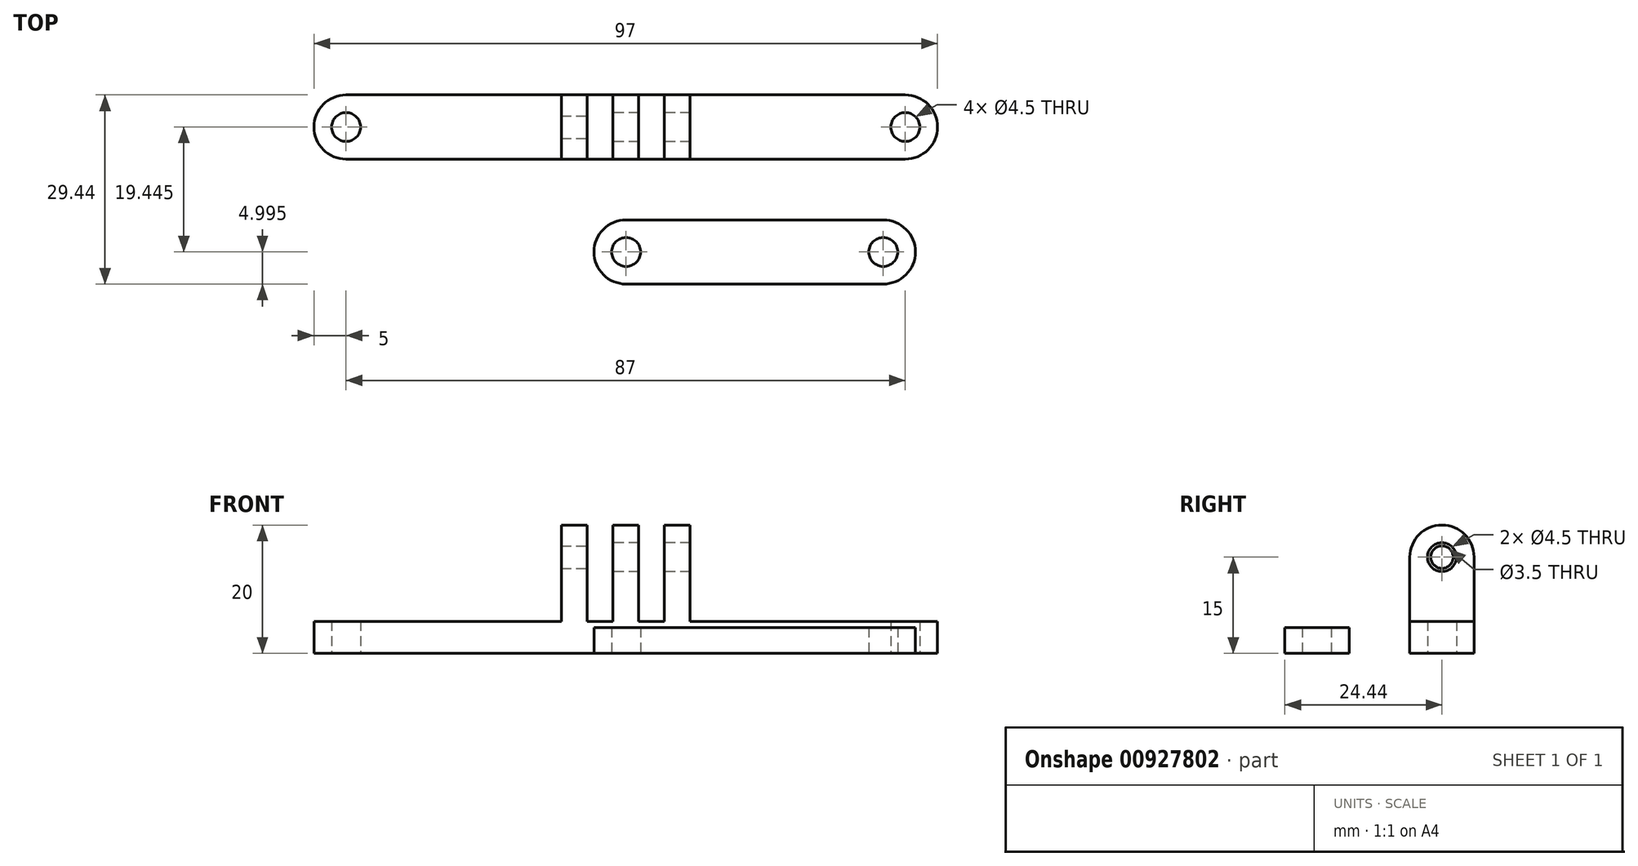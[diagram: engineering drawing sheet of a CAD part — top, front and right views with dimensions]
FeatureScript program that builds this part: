
annotation { "Feature Type Name" : "Feature", "Feature Type Description" : "" }
export const myFeature = defineFeature(function(context is Context, id is Id, definition is map)
    precondition{}
    {
        {
            var Q0;
            Q0=qCreatedBy(makeId("Front.planeOp"),FACE);
            var sketch = newSketch(context, id + "F0", { "sketchPlane" : qUnion([Q0])});
            skLineSegment(sketch, "E0.bottom", {"start": v(-48.5, 0) * mm, "end": v(48.5, 0) * mm});
            skLineSegment(sketch, "E0.top", {"start": v(-48.5, 5) * mm, "end": v(48.5, 5) * mm});
            skLineSegment(sketch, "E0.left", {"start": v(-48.5, 0) * mm, "end": v(-48.5, 5) * mm});
            skLineSegment(sketch, "E0.right", {"start": v(48.5, 0) * mm, "end": v(48.5, 5) * mm});
            skLineSegment(sketch, "E1.bottom", {"start": v(-10, 5) * mm, "end": v(-6, 5) * mm});
            skLineSegment(sketch, "E1.top", {"start": v(-10, 20) * mm, "end": v(-6, 20) * mm});
            skLineSegment(sketch, "E1.left", {"start": v(-10, 5) * mm, "end": v(-10, 20) * mm});
            skLineSegment(sketch, "E1.right", {"start": v(-6, 5) * mm, "end": v(-6, 20) * mm});
            skLineSegment(sketch, "E2.1.0.0", {"start": v(-2, 5) * mm, "end": v(-2, 20) * mm});
            skLineSegment(sketch, "E2.1.0.1", {"start": v(-2, 20) * mm, "end": v(2, 20) * mm});
            skLineSegment(sketch, "E2.1.0.2", {"start": v(2, 5) * mm, "end": v(2, 20) * mm});
            skLineSegment(sketch, "E2.2.0.0", {"start": v(6, 5) * mm, "end": v(6, 20) * mm});
            skLineSegment(sketch, "E2.2.0.1", {"start": v(6, 20) * mm, "end": v(10, 20) * mm});
            skLineSegment(sketch, "E2.2.0.2", {"start": v(10, 5) * mm, "end": v(10, 20) * mm});
            skLineSegment(sketch, "E2.direction1", {"start": v(-10, 5) * mm, "end": v(-2, 5) * mm, "construction": true});
            skLineSegment(sketch, "E3", {"start": v(0, 0) * mm, "end": v(0, 20) * mm, "construction": true});
            skSolve(sketch);
        }
        {
            var Q0;
            {var subQ0=sQuery(id+"F0.wireOp",EDGE,"E2.1.0.0");Q0=makeQuery(id+"F0.imprint","IMPRINT",FACE,{"disambiguationData":[TD([[makeQuery(id+"F0.imprint","IMPRINT",EDGE,{"derivedFrom":subQ0}),-1.0]])]});}
            var Q1;
            {var subQ0=sQuery(id+"F0.wireOp",EDGE,"E2.2.0.0");Q1=makeQuery(id+"F0.imprint","IMPRINT",FACE,{"disambiguationData":[TD([[makeQuery(id+"F0.imprint","IMPRINT",EDGE,{"derivedFrom":subQ0}),-1.0]])]});}
            var Q2;
            Q2=makeQuery(id+"F0.imprint","IMPRINT",FACE,{"disambiguationData":[TD([[makeQuery(id+"F0.imprint","IMPRINT",EDGE,{"derivedFrom":sQuery(id+"F0.wireOp",EDGE,"E1.top")}),-1.0]])]});
            var Q3;
            Q3=makeQuery(id+"F0.imprint","IMPRINT",FACE,{"disambiguationData":[TD([[makeQuery(id+"F0.imprint","IMPRINT",EDGE,{"derivedFrom":sQuery(id+"F0.wireOp",EDGE,"E0.bottom")}),1.0]])]});
            extrude(context, id + "F1", {"entities" : qUnion([Q0, Q1, Q2, Q3]), "endBound" : BoundingType.SYMMETRIC, "depth" : 10 * mm, "offsetDistance" : 25 * mm});
        }
        {
            var Q0;
            Q0=makeQuery(id+"F1.opExtrude","CAP_EDGE",EDGE,{"disambiguationData":[OSD([sQuery(id+"F0.wireOp",EDGE,"E0.left")])],"isStart":false});
            var Q1;
            Q1=makeQuery(id+"F1.opExtrude","CAP_EDGE",EDGE,{"disambiguationData":[OSD([sQuery(id+"F0.wireOp",EDGE,"E0.left")])],"isStart":true});
            var Q2;
            Q2=makeQuery(id+"F1.opExtrude","CAP_EDGE",EDGE,{"disambiguationData":[OSD([sQuery(id+"F0.wireOp",EDGE,"E0.right")])],"isStart":false});
            var Q3;
            Q3=makeQuery(id+"F1.opExtrude","CAP_EDGE",EDGE,{"disambiguationData":[OSD([sQuery(id+"F0.wireOp",EDGE,"E0.right")])],"isStart":true});
            var Q4;
            Q4=makeQuery(id+"F1.opExtrude","CAP_EDGE",EDGE,{"disambiguationData":[OSD([sQuery(id+"F0.wireOp",EDGE,"E1.top")])],"isStart":false});
            var Q5;
            Q5=makeQuery(id+"F1.opExtrude","CAP_EDGE",EDGE,{"disambiguationData":[OSD([sQuery(id+"F0.wireOp",EDGE,"E2.1.0.1")])],"isStart":false});
            var Q6;
            Q6=makeQuery(id+"F1.opExtrude","CAP_EDGE",EDGE,{"disambiguationData":[OSD([sQuery(id+"F0.wireOp",EDGE,"E2.2.0.1")])],"isStart":false});
            var Q7;
            Q7=makeQuery(id+"F1.opExtrude","CAP_EDGE",EDGE,{"disambiguationData":[OSD([sQuery(id+"F0.wireOp",EDGE,"E1.top")])],"isStart":true});
            var Q8;
            Q8=makeQuery(id+"F1.opExtrude","CAP_EDGE",EDGE,{"disambiguationData":[OSD([sQuery(id+"F0.wireOp",EDGE,"E2.1.0.1")])],"isStart":true});
            var Q9;
            Q9=makeQuery(id+"F1.opExtrude","CAP_EDGE",EDGE,{"disambiguationData":[OSD([sQuery(id+"F0.wireOp",EDGE,"E2.2.0.1")])],"isStart":true});
            fillet(context, id + "F2", {"entities" : qUnion([Q0, Q1, Q2, Q3, Q4, Q5, Q6, Q7, Q8, Q9]), "radius" : 5 * mm, "tangentPropagation" : true, "allowEdgeOverflow" : false});
        }
        {
            var Q0;
            Q0=makeQuery(id+"F1.opExtrude","SWEPT_FACE",FACE,{"disambiguationData":[OSD([sQuery(id+"F0.wireOp",EDGE,"E0.bottom")])]});
            var sketch = newSketch(context, id + "F3", { "sketchPlane" : qUnion([Q0])});
            skPoint(sketch, "E4", {"position": v(-43.5, 0) * mm});
            skPoint(sketch, "E5", {"position": v(43.5, 0) * mm});
            skLineSegment(sketch, "E6", {"start": v(0, 5) * mm, "end": v(0, -5) * mm, "construction": true});
            skSolve(sketch);
        }
        {
            var Q0;
            Q0=sQuery(id+"F3.wireOp",VERTEX,"E4");
            var Q1;
            Q1=sQuery(id+"F3.wireOp",VERTEX,"E5");
            var Q2;
            Q2=makeQuery(id+"F1.opExtrude","SWEPT_BODY",BODY,{"disambiguationData":[OSD([sQuery(id+"F0.wireOp",EDGE,"E0.bottom"),sQuery(id+"F0.wireOp",EDGE,"E0.top"),sQuery(id+"F0.wireOp",EDGE,"E0.left"),sQuery(id+"F0.wireOp",EDGE,"E0.right"),sQuery(id+"F0.wireOp",EDGE,"E1.top"),sQuery(id+"F0.wireOp",EDGE,"E1.left"),sQuery(id+"F0.wireOp",EDGE,"E1.right"),sQuery(id+"F0.wireOp",EDGE,"E2.1.0.0"),sQuery(id+"F0.wireOp",EDGE,"E2.1.0.1"),sQuery(id+"F0.wireOp",EDGE,"E2.1.0.2"),sQuery(id+"F0.wireOp",EDGE,"E2.2.0.0"),sQuery(id+"F0.wireOp",EDGE,"E2.2.0.1"),sQuery(id+"F0.wireOp",EDGE,"E2.2.0.2")])]});
            hole(context, id + "F4", {"style" : HoleStyle.SIMPLE, "endStyle" : HoleEndStyle.THROUGH, "standardTappedOrClearance" : lookupTablePath({ "fit" : "Normal", "standard" : "ISO", "size" : "M4", "type" : "Clearance" }), "standardBlindInLast" : lookupTablePath({ "fit" : "Normal", "standard" : "ISO", "engagement" : "75%", "pitch" : "0.7 mm", "size" : "M4", "type" : "Clearance & tapped" }), "holeDiameter" : 4.5 * mm, "majorDiameter" : 5 * mm, "isTappedThrough" : true, "tappedDepth" : 12 * mm, "tapClearance" : 3, "locations" : qUnion([Q0, Q1]), "scope" : qUnion([Q2])});
        }
        {
            var Q0;
            Q0=makeQuery(id+"F1.opExtrude","SWEPT_FACE",FACE,{"disambiguationData":[OSD([sQuery(id+"F0.wireOp",EDGE,"E2.1.0.0")])]});
            var sketch = newSketch(context, id + "F5", { "sketchPlane" : qUnion([Q0])});
            skPoint(sketch, "E7", {"position": v(0, 15) * mm});
            skSolve(sketch);
        }
        {
            var Q0;
            Q0=sQuery(id+"F5.wireOp",VERTEX,"E7");
            var Q1;
            Q1=makeQuery(id+"F1.opExtrude","SWEPT_BODY",BODY,{"disambiguationData":[OSD([sQuery(id+"F0.wireOp",EDGE,"E0.bottom"),sQuery(id+"F0.wireOp",EDGE,"E0.top"),sQuery(id+"F0.wireOp",EDGE,"E0.left"),sQuery(id+"F0.wireOp",EDGE,"E0.right"),sQuery(id+"F0.wireOp",EDGE,"E1.top"),sQuery(id+"F0.wireOp",EDGE,"E1.left"),sQuery(id+"F0.wireOp",EDGE,"E1.right"),sQuery(id+"F0.wireOp",EDGE,"E2.1.0.0"),sQuery(id+"F0.wireOp",EDGE,"E2.1.0.1"),sQuery(id+"F0.wireOp",EDGE,"E2.1.0.2"),sQuery(id+"F0.wireOp",EDGE,"E2.2.0.0"),sQuery(id+"F0.wireOp",EDGE,"E2.2.0.1"),sQuery(id+"F0.wireOp",EDGE,"E2.2.0.2")])]});
            hole(context, id + "F6", {"style" : HoleStyle.SIMPLE, "endStyle" : HoleEndStyle.THROUGH, "standardTappedOrClearance" : lookupTablePath({ "fit" : "Normal", "standard" : "ISO", "size" : "M4", "type" : "Clearance" }), "standardBlindInLast" : lookupTablePath({ "fit" : "Normal", "standard" : "ISO", "engagement" : "75%", "pitch" : "0.7 mm", "size" : "M4", "type" : "Clearance & tapped" }), "holeDiameter" : 4.5 * mm, "majorDiameter" : 5 * mm, "isTappedThrough" : true, "tappedDepth" : 12 * mm, "tapClearance" : 3, "locations" : qUnion([Q0]), "scope" : qUnion([Q1])});
        }
        {
            var Q0;
            Q0=sQuery(id+"F5.wireOp",VERTEX,"E7");
            var Q1;
            Q1=makeQuery(id+"F1.opExtrude","SWEPT_BODY",BODY,{"disambiguationData":[OSD([sQuery(id+"F0.wireOp",EDGE,"E0.bottom"),sQuery(id+"F0.wireOp",EDGE,"E0.top"),sQuery(id+"F0.wireOp",EDGE,"E0.left"),sQuery(id+"F0.wireOp",EDGE,"E0.right"),sQuery(id+"F0.wireOp",EDGE,"E1.top"),sQuery(id+"F0.wireOp",EDGE,"E1.left"),sQuery(id+"F0.wireOp",EDGE,"E1.right"),sQuery(id+"F0.wireOp",EDGE,"E2.1.0.0"),sQuery(id+"F0.wireOp",EDGE,"E2.1.0.1"),sQuery(id+"F0.wireOp",EDGE,"E2.1.0.2"),sQuery(id+"F0.wireOp",EDGE,"E2.2.0.0"),sQuery(id+"F0.wireOp",EDGE,"E2.2.0.1"),sQuery(id+"F0.wireOp",EDGE,"E2.2.0.2")])]});
            hole(context, id + "F7", {"style" : HoleStyle.SIMPLE, "endStyle" : HoleEndStyle.THROUGH, "oppositeDirection" : true, "standardTappedOrClearance" : lookupTablePath({ "standard" : "ISO", "size" : "3.5", "type" : "Drilled" }), "standardBlindInLast" : lookupTablePath({ "standard" : "ISO", "size" : "3.5", "type" : "Drilled" }), "holeDiameter" : 3.5 * mm, "majorDiameter" : 4 * mm, "isTappedThrough" : true, "tappedDepth" : 12 * mm, "tapClearance" : 3, "locations" : qUnion([Q0]), "scope" : qUnion([Q1])});
        }
        {
            var Q0;
            Q0=qCreatedBy(makeId("Top.planeOp"),FACE);
            var sketch = newSketch(context, id + "F8", { "sketchPlane" : qUnion([Q0])});
            skLineSegment(sketch, "E8.bottom", {"start": v(0.07, -14.44) * mm, "end": v(40.07, -14.44) * mm});
            skLineSegment(sketch, "E8.top", {"start": v(0.07, -24.44) * mm, "end": v(40.07, -24.44) * mm});
            skLineSegment(sketch, "E8.left", {"start": v(-4.93, -19.44) * mm, "end": v(-4.93, -19.44) * mm});
            skLineSegment(sketch, "E8.right", {"start": v(45.07, -19.44) * mm, "end": v(45.07, -19.44) * mm});
            skPoint(sketch, "E9.visualSharp", {"position": v(-4.93, -14.44) * mm});
            skArc(sketch, "E9.filletArc", {"start": v(0.07, -14.44) * mm, "mid": v(-3.47, -15.9) * mm, "end": v(-4.93, -19.44) * mm});
            skPoint(sketch, "E10.visualSharp", {"position": v(-4.93, -24.44) * mm});
            skArc(sketch, "E10.filletArc", {"start": v(-4.93, -19.44) * mm, "mid": v(-3.47, -22.98) * mm, "end": v(0.07, -24.44) * mm});
            skPoint(sketch, "E11.visualSharp", {"position": v(45.07, -14.44) * mm});
            skArc(sketch, "E11.filletArc", {"start": v(45.07, -19.44) * mm, "mid": v(43.6, -15.9) * mm, "end": v(40.07, -14.44) * mm});
            skPoint(sketch, "E12.visualSharp", {"position": v(45.07, -24.44) * mm});
            skArc(sketch, "E12.filletArc", {"start": v(40.07, -24.44) * mm, "mid": v(43.6, -22.98) * mm, "end": v(45.07, -19.44) * mm});
            skSolve(sketch);
        }
        {
            var Q0;
            Q0=makeQuery(id+"F8.imprint","IMPRINT",FACE,{"disambiguationData":[TD([[makeQuery(id+"F8.imprint","IMPRINT",EDGE,{"derivedFrom":sQuery(id+"F8.wireOp",EDGE,"E8.bottom")}),-1.0]])]});
            extrude(context, id + "F9", {"entities" : qUnion([Q0]), "depth" : 4 * mm, "offsetDistance" : 25 * mm});
        }
        {
            var Q0;
            Q0=sQuery(id+"F8.wireOp",VERTEX,"E9.filletArc.center");
            var Q1;
            Q1=sQuery(id+"F8.wireOp",VERTEX,"E11.filletArc.center");
            var Q2;
            Q2=makeQuery(id+"F9.opExtrude","SWEPT_BODY",BODY,{"disambiguationData":[OSD([sQuery(id+"F8.wireOp",EDGE,"E8.bottom"),sQuery(id+"F8.wireOp",EDGE,"E8.top"),sQuery(id+"F8.wireOp",EDGE,"E9.filletArc"),sQuery(id+"F8.wireOp",EDGE,"E10.filletArc"),sQuery(id+"F8.wireOp",EDGE,"E11.filletArc"),sQuery(id+"F8.wireOp",EDGE,"E12.filletArc")])]});
            hole(context, id + "F10", {"style" : HoleStyle.SIMPLE, "endStyle" : HoleEndStyle.THROUGH, "oppositeDirection" : true, "standardTappedOrClearance" : lookupTablePath({ "fit" : "Normal", "standard" : "ISO", "size" : "M4", "type" : "Clearance" }), "standardBlindInLast" : lookupTablePath({ "fit" : "Normal", "standard" : "ISO", "engagement" : "75%", "pitch" : "0.7 mm", "size" : "M4", "type" : "Clearance & tapped" }), "holeDiameter" : 4.5 * mm, "majorDiameter" : 5 * mm, "isTappedThrough" : true, "tappedDepth" : 12 * mm, "tapClearance" : 3, "locations" : qUnion([Q0, Q1]), "scope" : qUnion([Q2])});
        }
    });
